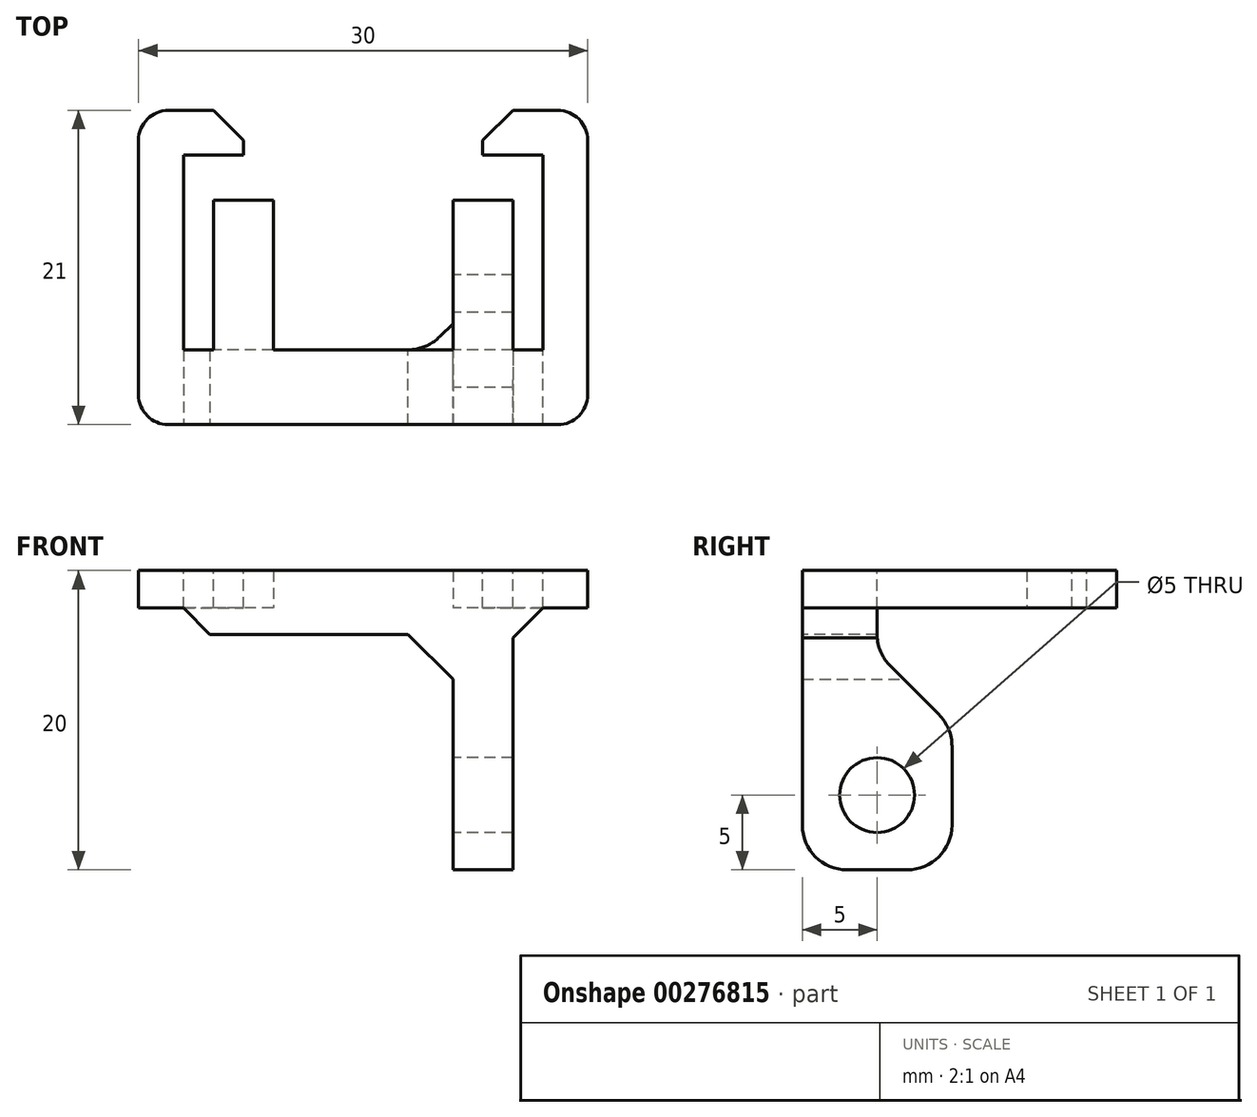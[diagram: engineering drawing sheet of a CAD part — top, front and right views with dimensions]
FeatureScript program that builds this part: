
annotation { "Feature Type Name" : "Feature", "Feature Type Description" : "" }
export const myFeature = defineFeature(function(context is Context, id is Id, definition is map)
    precondition{}
    {
        {
            var Q0;
            Q0=qCreatedBy(makeId("Top.planeOp"),FACE);
            var sketch = newSketch(context, id + "F0", { "sketchPlane" : qUnion([Q0])});
            skLineSegment(sketch, "E0", {"start": v(0, 0) * mm, "end": v(-6, 0) * mm});
            skLineSegment(sketch, "E1", {"start": v(-6, 0) * mm, "end": v(-6, 10) * mm});
            skLineSegment(sketch, "E2", {"start": v(-6, 10) * mm, "end": v(-10, 10) * mm});
            skLineSegment(sketch, "E3", {"start": v(-10, 10) * mm, "end": v(-10, -5) * mm});
            skLineSegment(sketch, "E4", {"start": v(-10, -5) * mm, "end": v(0, -5) * mm});
            skLineSegment(sketch, "E5", {"start": v(0, 0) * mm, "end": v(0, 21.9) * mm, "construction": true});
            skLineSegment(sketch, "E6.MirrorCS", {"start": v(0, 0) * mm, "end": v(6, 0) * mm});
            skLineSegment(sketch, "E7.MirrorCS", {"start": v(6, 0) * mm, "end": v(6, 10) * mm});
            skLineSegment(sketch, "E8.MirrorCS", {"start": v(10, 10) * mm, "end": v(10, -5) * mm});
            skLineSegment(sketch, "E9.MirrorCS", {"start": v(10, -5) * mm, "end": v(0, -5) * mm});
            skLineSegment(sketch, "E10.MirrorCS", {"start": v(6, 10) * mm, "end": v(10, 10) * mm});
            skSolve(sketch);
        }
        {
            var Q0;
            Q0 = qSketchRegion(id + "F0", true);
            extrude(context, id + "F1", {"entities" : qUnion([Q0]), "depth" : 2.5 * mm});
        }
        {
            var Q0;
            Q0=makeQuery(id+"F1.opExtrude","SWEPT_FACE",FACE,{"disambiguationData":[OSD([sQuery(id+"F0.wireOp",EDGE,"E3")])]});
            var sketch = newSketch(context, id + "F2", { "sketchPlane" : qUnion([Q0])});
            skLineSegment(sketch, "E11", {"start": v(0, 0) * mm, "end": v(0, -1.76) * mm});
            skLineSegment(sketch, "E12", {"start": v(-0.88, -3.88) * mm, "end": v(-4.12, -7.12) * mm});
            skLineSegment(sketch, "E13", {"start": v(-5, -9.24) * mm, "end": v(-5, -14.5) * mm});
            skLineSegment(sketch, "E14", {"start": v(-2, -17.5) * mm, "end": v(2, -17.5) * mm});
            skLineSegment(sketch, "E15", {"start": v(5, -14.5) * mm, "end": v(5, 0) * mm});
            skCircle(sketch, "E16", {"center": v(0, -12.5) * mm, "radius": 2.5 * mm});
            skPoint(sketch, "E17", {"position": v(0, -17.5) * mm});
            skPoint(sketch, "E18.visualSharp", {"position": v(5, -17.5) * mm});
            skArc(sketch, "E18.filletArc", {"start": v(2, -17.5) * mm, "mid": v(4.12, -16.62) * mm, "end": v(5, -14.5) * mm});
            skPoint(sketch, "E19.visualSharp", {"position": v(-5, -17.5) * mm});
            skArc(sketch, "E19.filletArc", {"start": v(-5, -14.5) * mm, "mid": v(-4.12, -16.62) * mm, "end": v(-2, -17.5) * mm});
            skPoint(sketch, "E20.visualSharp", {"position": v(-5, -8) * mm});
            skArc(sketch, "E20.filletArc", {"start": v(-4.12, -7.12) * mm, "mid": v(-4.77, -8.1) * mm, "end": v(-5, -9.24) * mm});
            skPoint(sketch, "E21.visualSharp", {"position": v(0, -3) * mm});
            skArc(sketch, "E21.filletArc", {"start": v(-0.88, -3.88) * mm, "mid": v(-0.23, -2.9) * mm, "end": v(0, -1.76) * mm});
            skLineSegment(sketch, "E22", {"start": v(5, 0) * mm, "end": v(0, 0) * mm});
            skSolve(sketch);
        }
        {
            var Q0;
            Q0 = qSketchRegion(id + "F2", true);
            var Q1;
            Q1=makeQuery(id+"F1.opExtrude","SWEPT_FACE",FACE,{"disambiguationData":[OSD([sQuery(id+"F0.wireOp",EDGE,"E8.MirrorCS")])]});
            extrude(context, id + "F3", {"entities" : qUnion([Q0]), "operationType" : NewBodyOperationType.ADD, "endBound" : BoundingType.UP_TO_SURFACE, "oppositeDirection" : true, "endBoundEntityFace" : qUnion([Q1]), "depth" : 25 * mm});
        }
        {
            var Q0;
            Q0=qCreatedBy(makeId("Front.planeOp"),FACE);
            var sketch = newSketch(context, id + "F4", { "sketchPlane" : qUnion([Q0])});
            skLineSegment(sketch, "E23", {"start": v(0, 0) * mm, "end": v(0, -4.16) * mm, "construction": true});
            skLineSegment(sketch, "E24", {"start": v(6, -17.5) * mm, "end": v(6, -4.76) * mm});
            skLineSegment(sketch, "E25", {"start": v(6, -4.76) * mm, "end": v(3, -1.76) * mm});
            skLineSegment(sketch, "E26", {"start": v(3, -1.76) * mm, "end": v(-10, -1.76) * mm});
            skLineSegment(sketch, "E27", {"start": v(-10, -1.76) * mm, "end": v(-10, -17.5) * mm});
            skLineSegment(sketch, "E28", {"start": v(-10, -17.5) * mm, "end": v(6, -17.5) * mm});
            skSolve(sketch);
        }
        {
            var Q0;
            Q0 = qSketchRegion(id + "F4", true);
            var Q1;
            Q1=makeQuery(id+"F3.boolean.opBoolean","MERGE",FACE,{"derivedFrom":[makeQuery(id+"F1.opExtrude","SWEPT_FACE",FACE,{"disambiguationData":[OSD([sQuery(id+"F0.wireOp",EDGE,"E4"),sQuery(id+"F0.wireOp",EDGE,"E9.MirrorCS")])]}),makeQuery(id+"F3.opExtrude","SWEPT_FACE",FACE,{"disambiguationData":[OSD([sQuery(id+"F2.wireOp",EDGE,"E15")])]})]});
            extrude(context, id + "F5", {"entities" : qUnion([Q0]), "operationType" : NewBodyOperationType.REMOVE, "endBound" : BoundingType.THROUGH_ALL, "endBoundEntityFace" : qUnion([Q1]), "depth" : 25 * mm, "hasSecondDirection" : true, "secondDirectionBound" : SecondDirectionBoundingType.THROUGH_ALL, "secondDirectionOppositeDirection" : true, "secondDirectionDepth" : 25 * mm});
        }
        {
            var Q0;
            Q0=makeQuery(id+"F1.opExtrude","CAP_FACE",FACE,{"disambiguationData":[OSD([sQuery(id+"F0.wireOp",EDGE,"E0"),sQuery(id+"F0.wireOp",EDGE,"E1"),sQuery(id+"F0.wireOp",EDGE,"E2"),sQuery(id+"F0.wireOp",EDGE,"E3"),sQuery(id+"F0.wireOp",EDGE,"E4"),sQuery(id+"F0.wireOp",EDGE,"E6.MirrorCS"),sQuery(id+"F0.wireOp",EDGE,"E7.MirrorCS"),sQuery(id+"F0.wireOp",EDGE,"E8.MirrorCS"),sQuery(id+"F0.wireOp",EDGE,"E9.MirrorCS"),sQuery(id+"F0.wireOp",EDGE,"E10.MirrorCS")])],"isStart":false});
            var sketch = newSketch(context, id + "F6", { "sketchPlane" : qUnion([Q0])});
            skLineSegment(sketch, "E29", {"start": v(-10, -5) * mm, "end": v(-13, -5) * mm});
            skLineSegment(sketch, "E30", {"start": v(-15, -3) * mm, "end": v(-15, 14) * mm});
            skLineSegment(sketch, "E31", {"start": v(-13, 16) * mm, "end": v(-10, 16) * mm});
            skLineSegment(sketch, "E32", {"start": v(-10, 16) * mm, "end": v(-8, 14) * mm});
            skLineSegment(sketch, "E33", {"start": v(-8, 14) * mm, "end": v(-8, 13) * mm});
            skLineSegment(sketch, "E34", {"start": v(-8, 13) * mm, "end": v(-12, 13) * mm});
            skLineSegment(sketch, "E35", {"start": v(-12, 13) * mm, "end": v(-12, 0) * mm});
            skLineSegment(sketch, "E36", {"start": v(-12, 0) * mm, "end": v(-10, 0) * mm});
            skLineSegment(sketch, "E37", {"start": v(-10, 0) * mm, "end": v(-10, -5) * mm});
            skPoint(sketch, "E38.visualSharp", {"position": v(-15, -5) * mm});
            skArc(sketch, "E38.filletArc", {"start": v(-15, -3) * mm, "mid": v(-14.41, -4.41) * mm, "end": v(-13, -5) * mm});
            skPoint(sketch, "E39.visualSharp", {"position": v(-15, 16) * mm});
            skArc(sketch, "E39.filletArc", {"start": v(-13, 16) * mm, "mid": v(-14.41, 15.41) * mm, "end": v(-15, 14) * mm});
            skLineSegment(sketch, "E40", {"start": v(0, 0) * mm, "end": v(0, 11.68) * mm, "construction": true});
            skPoint(sketch, "E40.endSnap0", {"position": v(0, 0) * mm});
            skLineSegment(sketch, "E41.MirrorCS", {"start": v(8, 14) * mm, "end": v(8, 13) * mm});
            skLineSegment(sketch, "E42.MirrorCS", {"start": v(10, 0) * mm, "end": v(10, -5) * mm});
            skArc(sketch, "E43.MirrorCS", {"start": v(15, -3) * mm, "mid": v(14.41, -4.41) * mm, "end": v(13, -5) * mm});
            skPoint(sketch, "E44.MirrorP", {"position": v(15, 16) * mm});
            skPoint(sketch, "E45.MirrorP", {"position": v(15, -5) * mm});
            skLineSegment(sketch, "E46.MirrorCS", {"start": v(10, -5) * mm, "end": v(13, -5) * mm});
            skLineSegment(sketch, "E47.MirrorCS", {"start": v(10, 16) * mm, "end": v(8, 14) * mm});
            skLineSegment(sketch, "E48.MirrorCS", {"start": v(12, 13) * mm, "end": v(12, 0) * mm});
            skLineSegment(sketch, "E49.MirrorCS", {"start": v(15, -3) * mm, "end": v(15, 14) * mm});
            skLineSegment(sketch, "E50.MirrorCS", {"start": v(13, 16) * mm, "end": v(10, 16) * mm});
            skLineSegment(sketch, "E51.MirrorCS", {"start": v(12, 0) * mm, "end": v(10, 0) * mm});
            skLineSegment(sketch, "E52.MirrorCS", {"start": v(8, 13) * mm, "end": v(12, 13) * mm});
            skArc(sketch, "E53.MirrorCS", {"start": v(13, 16) * mm, "mid": v(14.41, 15.41) * mm, "end": v(15, 14) * mm});
            skSolve(sketch);
        }
        {
            var Q0;
            Q0 = qSketchRegion(id + "F6", true);
            var Q1;
            {var subQ0=sQuery(id+"F0.wireOp",EDGE,"E3");var subQ1=sQuery(id+"F0.wireOp",EDGE,"E2");var subQ3=sQuery(id+"F0.wireOp",EDGE,"E1");var subQ4=sQuery(id+"F0.wireOp",EDGE,"E6.MirrorCS");var subQ5=sQuery(id+"F0.wireOp",EDGE,"E0");Q1=makeQuery(id+"F3.boolean.opBoolean","SPLIT",FACE,{"disambiguationData":[TD([makeQuery(id+"F1.opExtrude","SWEPT_FACE",FACE,{"disambiguationData":[OSD([subQ3])]})])],"derivedFrom":makeQuery(id+"F1.opExtrude","CAP_FACE",FACE,{"disambiguationData":[OSD([subQ5,subQ3,subQ1,subQ0,sQuery(id+"F0.wireOp",EDGE,"E4"),subQ4,sQuery(id+"F0.wireOp",EDGE,"E7.MirrorCS"),sQuery(id+"F0.wireOp",EDGE,"E8.MirrorCS"),sQuery(id+"F0.wireOp",EDGE,"E9.MirrorCS"),sQuery(id+"F0.wireOp",EDGE,"E10.MirrorCS")])],"isStart":true})});}
            extrude(context, id + "F7", {"entities" : qUnion([Q0]), "operationType" : NewBodyOperationType.ADD, "endBound" : BoundingType.UP_TO_SURFACE, "oppositeDirection" : true, "endBoundEntityFace" : qUnion([Q1]), "depth" : 25 * mm});
        }
        {
            var Q0;
            Q0=makeQuery(id+"F7.opExtrude","CAP_EDGE",EDGE,{"disambiguationData":[OSD([sQuery(id+"F6.wireOp",EDGE,"E37")])],"isStart":false});
            var Q1;
            Q1=makeQuery(id+"F7.opExtrude","CAP_EDGE",EDGE,{"disambiguationData":[OSD([sQuery(id+"F6.wireOp",EDGE,"E42.MirrorCS")])],"isStart":false});
            chamfer(context, id + "F8", {"entities" : qUnion([Q0, Q1]), "width" : 2 * mm, "tangentPropagation" : true});
        }
    });
